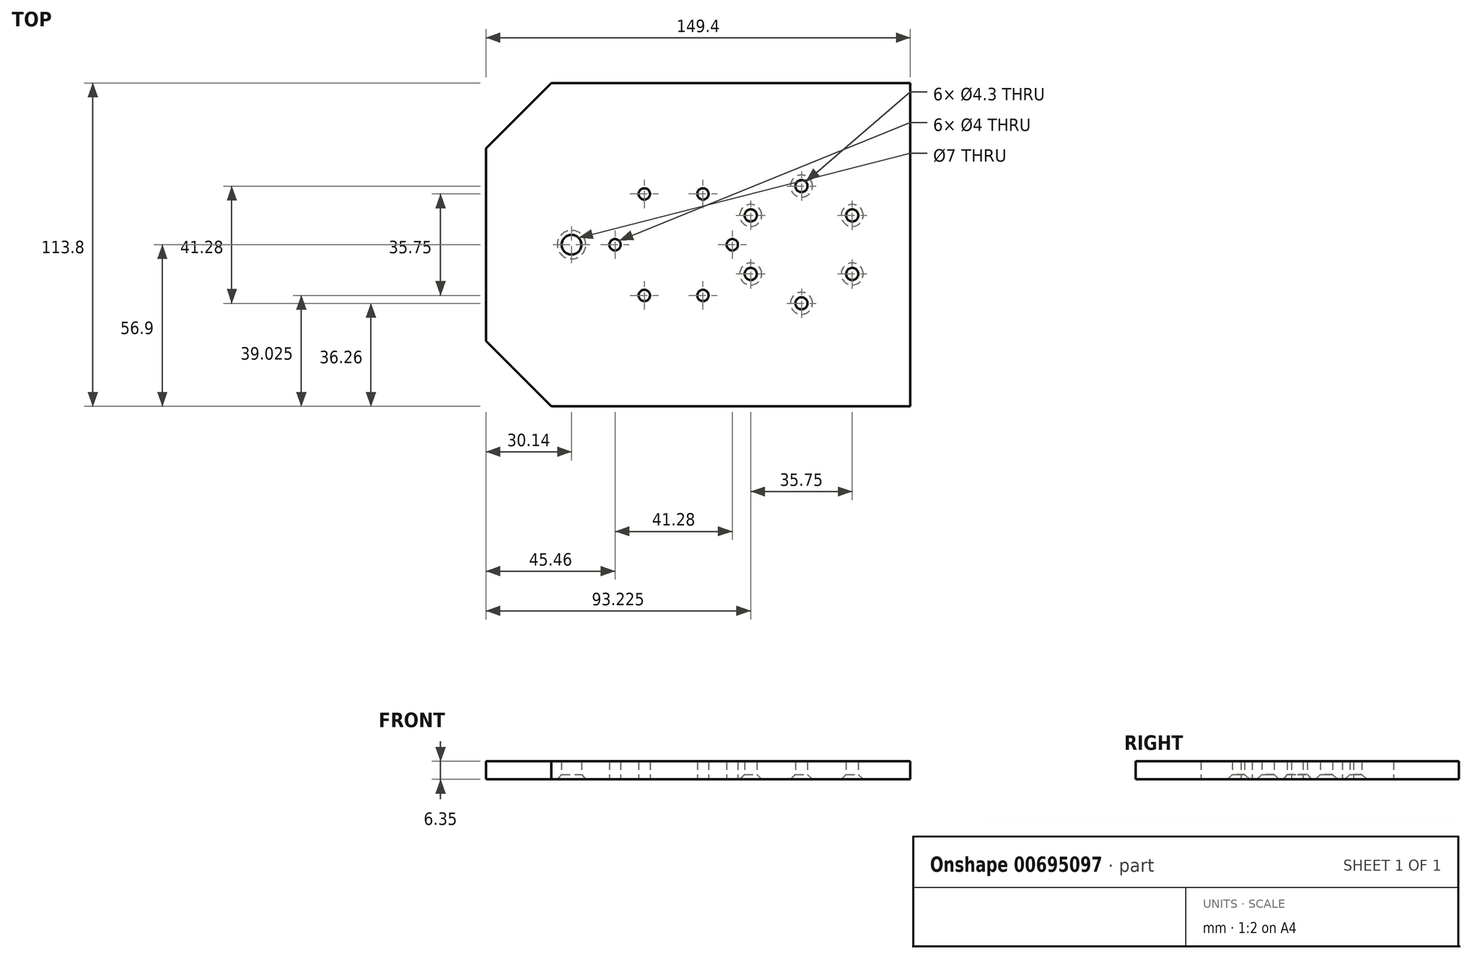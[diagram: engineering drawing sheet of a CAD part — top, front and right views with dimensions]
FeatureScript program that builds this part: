
annotation { "Feature Type Name" : "Feature", "Feature Type Description" : "" }
export const myFeature = defineFeature(function(context is Context, id is Id, definition is map)
    precondition{}
    {
        {
            var Q0;
            Q0=qCreatedBy(makeId("Top.planeOp"),FACE);
            var sketch = newSketch(context, id + "F0", { "sketchPlane" : qUnion([Q0])});
            skLineSegment(sketch, "E0.bottom", {"start": v(-126.4, 0) * mm, "end": v(0, 0) * mm});
            skLineSegment(sketch, "E0.top", {"start": v(-126.4, 113.8) * mm, "end": v(0, 113.8) * mm});
            skLineSegment(sketch, "E0.left", {"start": v(-149.4, 23) * mm, "end": v(-149.4, 90.8) * mm});
            skLineSegment(sketch, "E0.right", {"start": v(0, 0) * mm, "end": v(0, 113.8) * mm});
            skLineSegment(sketch, "E1", {"start": v(-126.4, 113.8) * mm, "end": v(-149.4, 90.8) * mm});
            skLineSegment(sketch, "E2", {"start": v(-149.4, 23) * mm, "end": v(-126.4, 0) * mm});
            skLineSegment(sketch, "E3", {"start": v(0, 56.9) * mm, "end": v(-149.4, 56.9) * mm, "construction": true});
            skCircle(sketch, "E4", {"center": v(-38.3, 56.9) * mm, "radius": 20.64 * mm, "construction": true});
            skCircle(sketch, "E5", {"center": v(-83.3, 56.9) * mm, "radius": 20.64 * mm, "construction": true});
            skPoint(sketch, "E6", {"position": v(-119.26, 56.9) * mm});
            skPoint(sketch, "E7", {"position": v(-103.94, 56.9) * mm});
            skPoint(sketch, "E8", {"position": v(-38.3, 36.26) * mm});
            skPoint(sketch, "E9.1.0", {"position": v(-93.62, 39.03) * mm});
            skPoint(sketch, "E9.2.0", {"position": v(-72.98, 39.03) * mm});
            skPoint(sketch, "E9.3.0", {"position": v(-62.66, 56.9) * mm});
            skPoint(sketch, "E9.4.0", {"position": v(-72.98, 74.77) * mm});
            skPoint(sketch, "E9.5.0", {"position": v(-93.62, 74.77) * mm});
            skPoint(sketch, "E10.1.0", {"position": v(-20.43, 46.58) * mm});
            skPoint(sketch, "E10.2.0", {"position": v(-20.43, 67.22) * mm});
            skPoint(sketch, "E10.3.0", {"position": v(-38.3, 77.54) * mm});
            skPoint(sketch, "E10.4.0", {"position": v(-56.17, 67.22) * mm});
            skPoint(sketch, "E10.5.0", {"position": v(-56.17, 46.58) * mm});
            skLineSegment(sketch, "E11", {"start": v(-38.3, 56.9) * mm, "end": v(-20.43, 46.58) * mm, "construction": true});
            skSolve(sketch);
        }
        {
            var Q0;
            Q0=makeQuery(id+"F0.imprint","IMPRINT",FACE,{"disambiguationData":[TD([[makeQuery(id+"F0.imprint","IMPRINT",EDGE,{"derivedFrom":sQuery(id+"F0.wireOp",EDGE,"E0.bottom")}),1.0]])]});
            extrude(context, id + "F1", {"entities" : qUnion([Q0]), "depth" : 6.35 * mm, "offsetDistance" : 25 * mm});
        }
        {
            var Q0;
            Q0=sQuery(id+"F0.wireOp",VERTEX,"E6");
            var Q1;
            Q1=makeQuery(id+"F1.opExtrude","SWEPT_BODY",BODY,{"disambiguationData":[OSD([sQuery(id+"F0.wireOp",EDGE,"E0.bottom"),sQuery(id+"F0.wireOp",EDGE,"E0.top"),sQuery(id+"F0.wireOp",EDGE,"E0.left"),sQuery(id+"F0.wireOp",EDGE,"E0.right"),sQuery(id+"F0.wireOp",EDGE,"E1"),sQuery(id+"F0.wireOp",EDGE,"E2")])]});
            hole(context, id + "F2", {"style" : HoleStyle.C_SINK, "endStyle" : HoleEndStyle.THROUGH, "oppositeDirection" : true, "holeDiameter" : 7 * mm, "cSinkDiameter" : 10 * mm, "cSinkAngle" : 82 * degree, "majorDiameter" : 5 * mm, "isTappedThrough" : true, "tappedDepth" : 12 * mm, "tapClearance" : 3, "locations" : qUnion([Q0]), "scope" : qUnion([Q1])});
        }
        {
            var Q0;
            Q0=sQuery(id+"F0.wireOp",VERTEX,"E8");
            var Q1;
            Q1=sQuery(id+"F0.wireOp",VERTEX,"E10.1.0");
            var Q2;
            Q2=sQuery(id+"F0.wireOp",VERTEX,"E10.2.0");
            var Q3;
            Q3=sQuery(id+"F0.wireOp",VERTEX,"E10.3.0");
            var Q4;
            Q4=sQuery(id+"F0.wireOp",VERTEX,"E10.4.0");
            var Q5;
            Q5=sQuery(id+"F0.wireOp",VERTEX,"E10.5.0");
            var Q6;
            Q6=makeQuery(id+"F1.opExtrude","SWEPT_BODY",BODY,{"disambiguationData":[OSD([sQuery(id+"F0.wireOp",EDGE,"E0.bottom"),sQuery(id+"F0.wireOp",EDGE,"E0.top"),sQuery(id+"F0.wireOp",EDGE,"E0.left"),sQuery(id+"F0.wireOp",EDGE,"E0.right"),sQuery(id+"F0.wireOp",EDGE,"E1"),sQuery(id+"F0.wireOp",EDGE,"E2")])]});
            hole(context, id + "F3", {"style" : HoleStyle.C_SINK, "endStyle" : HoleEndStyle.THROUGH, "oppositeDirection" : true, "holeDiameter" : 4.3 * mm, "cSinkDiameter" : 7.75 * mm, "cSinkAngle" : 90 * degree, "majorDiameter" : 5 * mm, "isTappedThrough" : true, "tappedDepth" : 12 * mm, "tapClearance" : 3, "locations" : qUnion([Q0, Q1, Q2, Q3, Q4, Q5]), "scope" : qUnion([Q6])});
        }
        {
            var Q0;
            Q0=sQuery(id+"F0.wireOp",VERTEX,"E7");
            var Q1;
            Q1=sQuery(id+"F0.wireOp",VERTEX,"E9.1.0");
            var Q2;
            Q2=sQuery(id+"F0.wireOp",VERTEX,"E9.2.0");
            var Q3;
            Q3=sQuery(id+"F0.wireOp",VERTEX,"E9.3.0");
            var Q4;
            Q4=sQuery(id+"F0.wireOp",VERTEX,"E9.4.0");
            var Q5;
            Q5=sQuery(id+"F0.wireOp",VERTEX,"E9.5.0");
            var Q6;
            Q6=makeQuery(id+"F1.opExtrude","SWEPT_BODY",BODY,{"disambiguationData":[OSD([sQuery(id+"F0.wireOp",EDGE,"E0.bottom"),sQuery(id+"F0.wireOp",EDGE,"E0.top"),sQuery(id+"F0.wireOp",EDGE,"E0.left"),sQuery(id+"F0.wireOp",EDGE,"E0.right"),sQuery(id+"F0.wireOp",EDGE,"E1"),sQuery(id+"F0.wireOp",EDGE,"E2")])]});
            hole(context, id + "F4", {"style" : HoleStyle.SIMPLE, "endStyle" : HoleEndStyle.THROUGH, "oppositeDirection" : true, "holeDiameter" : 4 * mm, "majorDiameter" : 5 * mm, "isTappedThrough" : true, "tappedDepth" : 12 * mm, "tapClearance" : 3, "locations" : qUnion([Q0, Q1, Q2, Q3, Q4, Q5]), "scope" : qUnion([Q6])});
        }
    });
